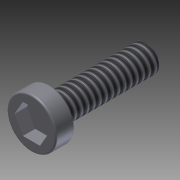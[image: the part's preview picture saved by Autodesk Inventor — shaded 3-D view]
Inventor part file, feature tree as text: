
AUTODESK INVENTOR PART (.ipt)
format: ipt  version: 2012 (Build 160160000, 160)  size: 118,272 bytes
history: native  units: in
note: dims shown in document units (in); Inventor stores cm internally (conversion verified against a paired STEP export)
features: extrude x3, sketch x1, thread x1, chamfer x1, fillet x1
ambient origin geometry x8: Origin, YZ Plane, XZ Plane, XY Plane, X Axis, Y Axis, Z Axis, Center Point
bodies: Solid1 (feature_tree)
feature tree (7):
  sketch  "Sketch1"  dims[d0=0.136in d1=0.25in d2=0.15in d3=0.5in d4=0.0in d5=0.0938in d6=0.0in d7=0.0312in d8=0.0in d9=1.0in d10=0.0in d11=0.0156in d12=0.125in d13=45.0deg d14=0.0078in]
  extrude  "Extrusion1"  Depth=0.25in
  extrude  "Extrusion2"  Depth=0.15in
  extrude  "Extrusion3"  Depth=0.5in TaperAngle=0.0deg
  thread  "Thread1"  [1 undecoded]
  chamfer  "Chamfer1"  Distance=0.0312in
  fillet  "Fillet1"  Radius=1.0in
note: 1 required parameter value undecoded (feature->parameter linkage not recoverable at this tier; creation-order binding heuristic only, values carry confidence <= 0.55)
